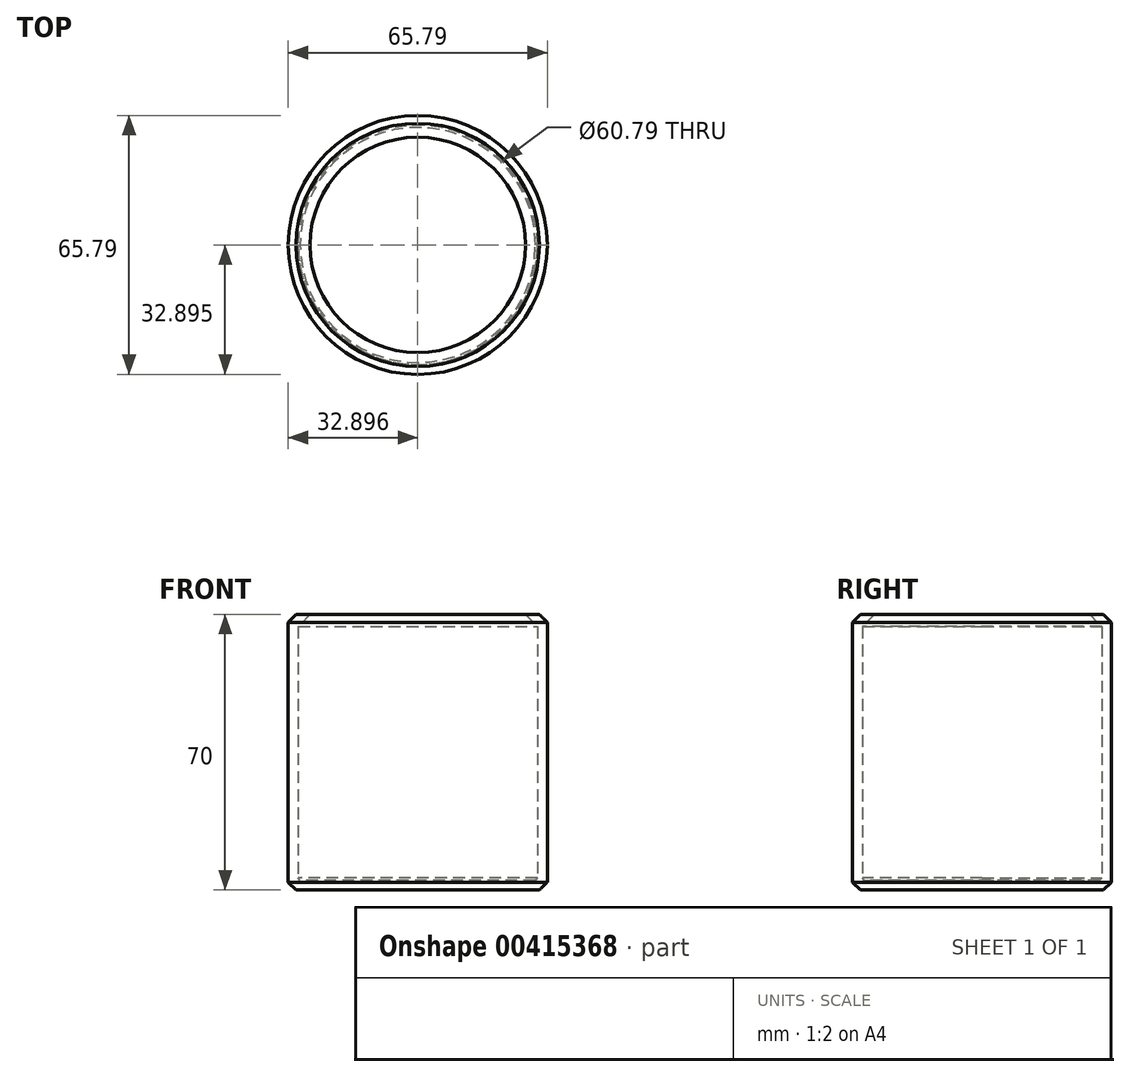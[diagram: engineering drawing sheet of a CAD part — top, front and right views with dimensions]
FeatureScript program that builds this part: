
annotation { "Feature Type Name" : "Feature", "Feature Type Description" : "" }
export const myFeature = defineFeature(function(context is Context, id is Id, definition is map)
    precondition{}
    {
        {
            var Q0;
            Q0=qCreatedBy(makeId("Top.planeOp"),FACE);
            var sketch = newSketch(context, id + "F0", { "sketchPlane" : qUnion([Q0])});
            skCircle(sketch, "E0", {"center": v(-31.05, 27.46) * mm, "radius": 32.9 * mm});
            skSolve(sketch);
        }
        {
            var Q0;
            Q0=makeQuery(id+"F0.imprint","IMPRINT",FACE,{"disambiguationData":[TD([[makeQuery(id+"F0.imprint","IMPRINT",EDGE,{"derivedFrom":sQuery(id+"F0.wireOp",EDGE,"E0")}),1.0]])]});
            extrude(context, id + "F1", {"entities" : qUnion([Q0]), "depth" : 70 * mm});
        }
        {
            var Q0;
            Q0=makeQuery(id+"F1.opExtrude","CAP_FACE",FACE,{"disambiguationData":[OSD([sQuery(id+"F0.wireOp",EDGE,"E0")])],"isStart":false});
            chamfer(context, id + "F2", {"entities" : qUnion([Q0]), "width" : 2 * mm, "tangentPropagation" : true});
        }
        {
            var Q0;
            Q0=makeQuery(id+"F1.opExtrude","CAP_FACE",FACE,{"disambiguationData":[OSD([sQuery(id+"F0.wireOp",EDGE,"E0")])],"isStart":true});
            chamfer(context, id + "F3", {"entities" : qUnion([Q0]), "width" : 2 * mm, "tangentPropagation" : true});
        }
        {
            var Q0;
            Q0=makeQuery(id+"F1.opExtrude","CAP_FACE",FACE,{"disambiguationData":[OSD([sQuery(id+"F0.wireOp",EDGE,"E0")])],"isStart":false});
            shell(context, id + "F4", {"entities" : qUnion([Q0]), "thickness" : 2.5 * mm});
        }
    });
